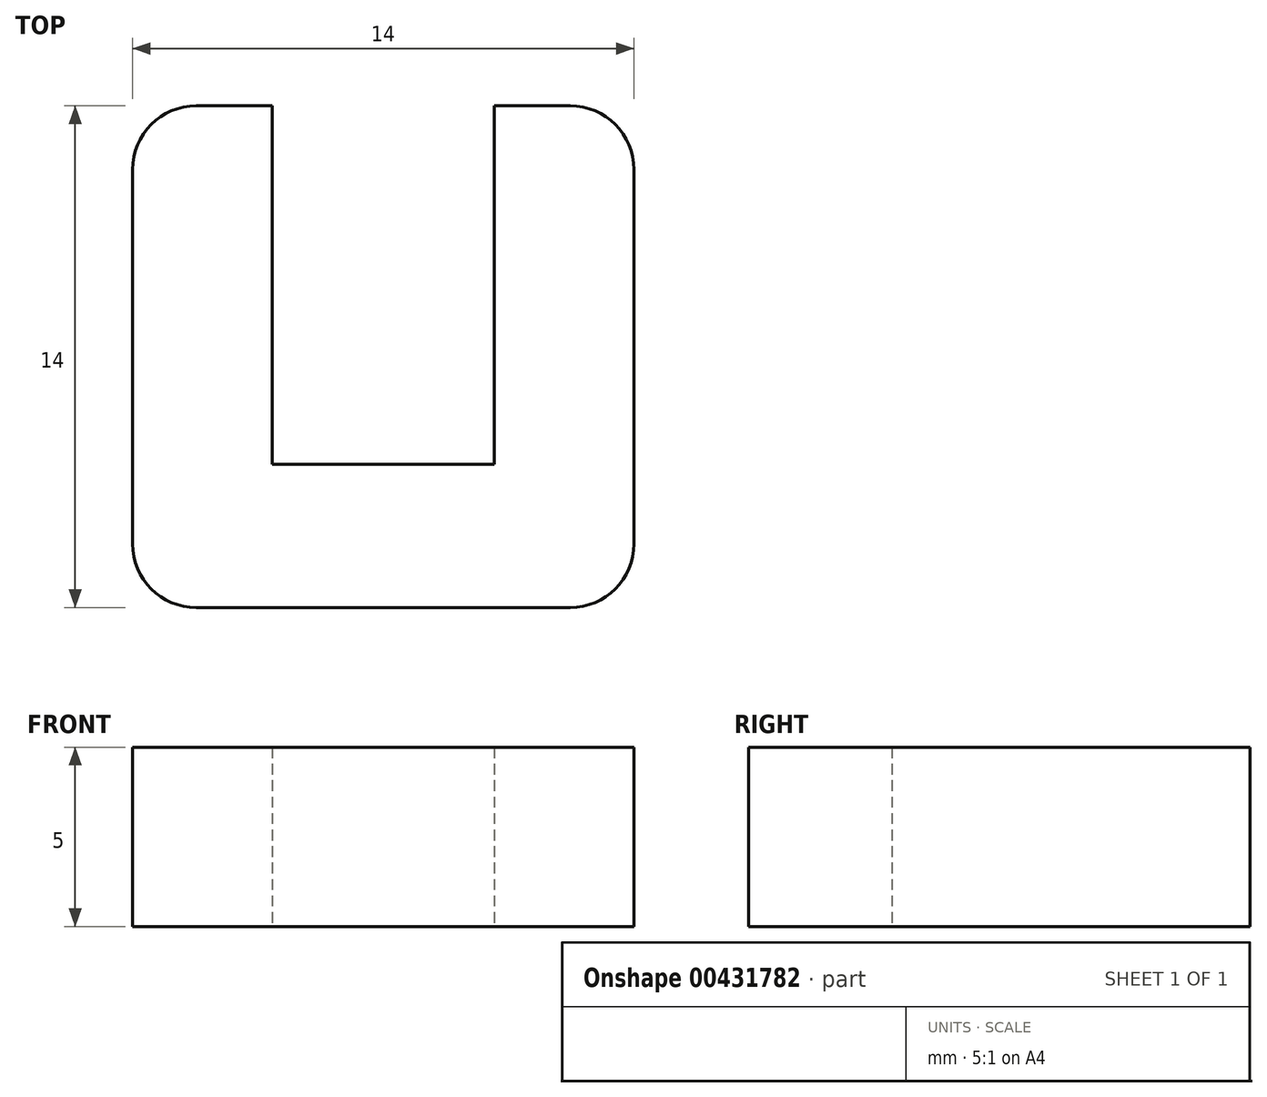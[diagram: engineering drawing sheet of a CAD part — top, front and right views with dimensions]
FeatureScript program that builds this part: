
annotation { "Feature Type Name" : "Feature", "Feature Type Description" : "" }
export const myFeature = defineFeature(function(context is Context, id is Id, definition is map)
    precondition{}
    {
        {
            var Q0;
            Q0=qCreatedBy(makeId("Top.planeOp"),FACE);
            var sketch = newSketch(context, id + "F0", { "sketchPlane" : qUnion([Q0])});
            skLineSegment(sketch, "E0", {"start": v(0, 1.78) * mm, "end": v(0, 12.22) * mm});
            skLineSegment(sketch, "E1", {"start": v(1.78, 0) * mm, "end": v(12.22, 0) * mm});
            skLineSegment(sketch, "E2", {"start": v(14, 1.78) * mm, "end": v(14, 12.22) * mm});
            skLineSegment(sketch, "E3", {"start": v(12.22, 14) * mm, "end": v(10.1, 14) * mm});
            skLineSegment(sketch, "E4", {"start": v(10.1, 14) * mm, "end": v(10.1, 4) * mm});
            skLineSegment(sketch, "E5", {"start": v(10.1, 4) * mm, "end": v(3.9, 4) * mm});
            skLineSegment(sketch, "E6", {"start": v(3.9, 4) * mm, "end": v(3.9, 14) * mm});
            skLineSegment(sketch, "E7", {"start": v(3.9, 14) * mm, "end": v(1.78, 14) * mm});
            skPoint(sketch, "E8.visualSharp", {"position": v(14, 0) * mm});
            skArc(sketch, "E8.filletArc", {"start": v(12.22, 0) * mm, "mid": v(13.48, 0.52) * mm, "end": v(14, 1.78) * mm});
            skPoint(sketch, "E9.visualSharp", {"position": v(0, 0) * mm});
            skArc(sketch, "E9.filletArc", {"start": v(0, 1.78) * mm, "mid": v(0.52, 0.52) * mm, "end": v(1.78, 0) * mm});
            skPoint(sketch, "E10.visualSharp", {"position": v(0, 14) * mm});
            skArc(sketch, "E10.filletArc", {"start": v(1.78, 14) * mm, "mid": v(0.52, 13.48) * mm, "end": v(0, 12.22) * mm});
            skPoint(sketch, "E11.visualSharp", {"position": v(14, 14) * mm});
            skArc(sketch, "E11.filletArc", {"start": v(14, 12.22) * mm, "mid": v(13.48, 13.48) * mm, "end": v(12.22, 14) * mm});
            skSolve(sketch);
        }
        {
            var Q0;
            Q0 = qSketchRegion(id + "F0", true);
            extrude(context, id + "F1", {"entities" : qUnion([Q0]), "depth" : 5 * mm});
        }
    });
